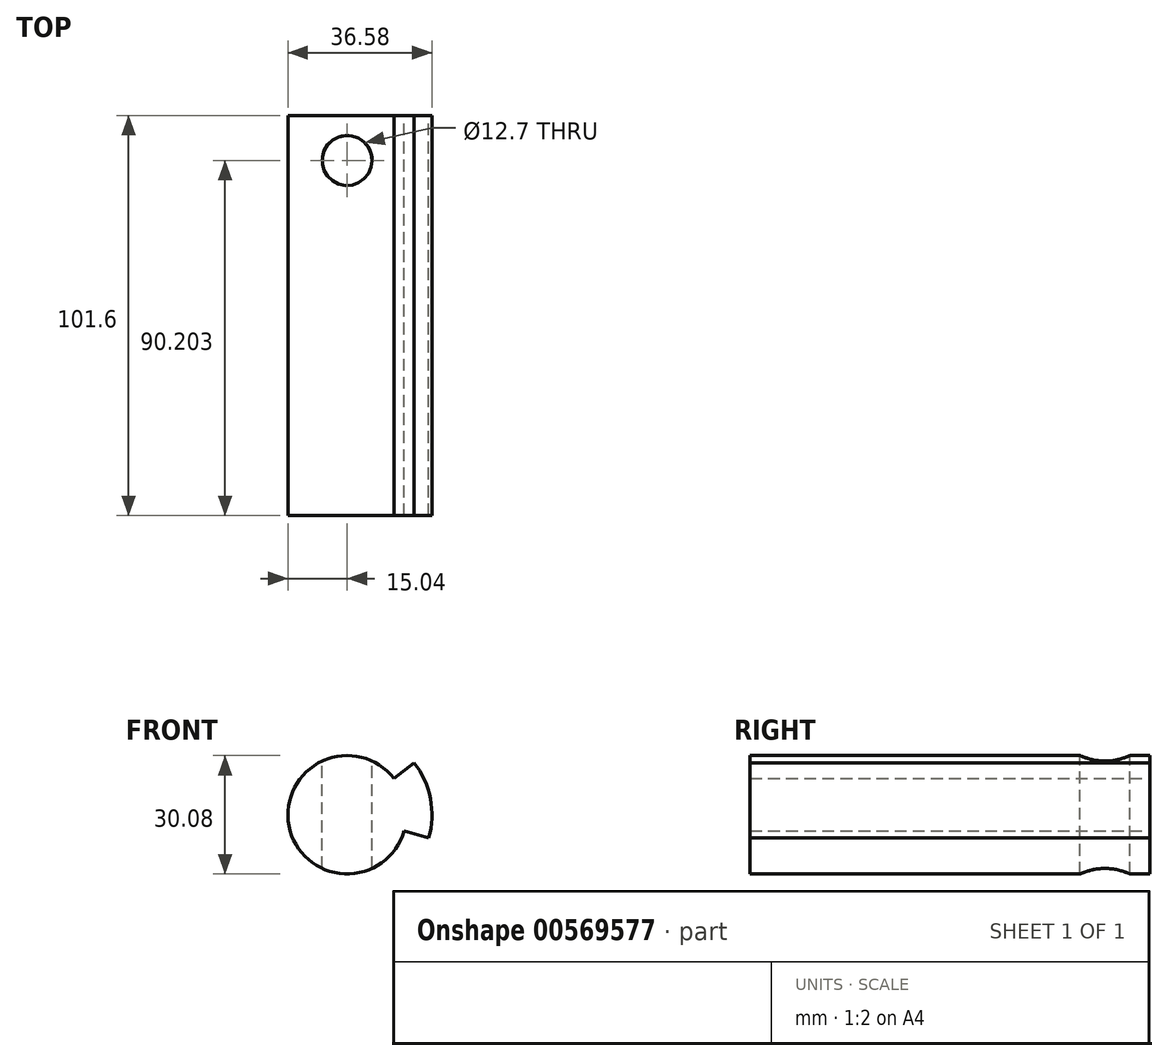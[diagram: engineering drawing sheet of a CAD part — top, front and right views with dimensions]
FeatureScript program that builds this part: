
annotation { "Feature Type Name" : "Feature", "Feature Type Description" : "" }
export const myFeature = defineFeature(function(context is Context, id is Id, definition is map)
    precondition{}
    {
        {
            var Q0;
            Q0=qCreatedBy(makeId("Front.planeOp"),FACE);
            var sketch = newSketch(context, id + "F0", { "sketchPlane" : qUnion([Q0])});
            skArc(sketch, "E0", {"start": v(11.89, 9.2) * mm, "mid": v(-14.76, -2.85) * mm, "end": v(14.46, -4.13) * mm});
            skArc(sketch, "E1.0", {"start": v(20.71, -5.91) * mm, "mid": v(21.15, 4.08) * mm, "end": v(17.03, 13.2) * mm});
            skLineSegment(sketch, "E2", {"start": v(11.89, 9.2) * mm, "end": v(17.03, 13.2) * mm});
            skLineSegment(sketch, "E3", {"start": v(14.46, -4.13) * mm, "end": v(20.71, -5.91) * mm});
            skSolve(sketch);
        }
        {
            var Q0;
            Q0=makeQuery(id+"F0.imprint","IMPRINT",FACE,{"disambiguationData":[TD([[makeQuery(id+"F0.imprint","IMPRINT",EDGE,{"derivedFrom":sQuery(id+"F0.wireOp",EDGE,"E0")}),1.0]])]});
            extrude(context, id + "F1", {"entities" : qUnion([Q0]), "endBound" : BoundingType.SYMMETRIC, "depth" : 101.6 * mm, "offsetDistance" : 25.4 * mm});
        }
        {
            var Q0;
            Q0=qCreatedBy(makeId("Top.planeOp"),FACE);
            var sketch = newSketch(context, id + "F2", { "sketchPlane" : qUnion([Q0])});
            skCircle(sketch, "E4", {"center": v(0, 39.4) * mm, "radius": 6.35 * mm});
            skLineSegment(sketch, "E5", {"start": v(-15.04, -50.8) * mm, "end": v(-15.04, 50.8) * mm});
            skSolve(sketch);
        }
        {
            var Q0;
            Q0 = qSketchRegion(id + "F2", true);
            extrude(context, id + "F3", {"entities" : qUnion([Q0]), "operationType" : NewBodyOperationType.REMOVE, "endBound" : BoundingType.THROUGH_ALL, "oppositeDirection" : true, "depth" : 25.4 * mm, "offsetDistance" : 25.4 * mm, "hasSecondDirection" : true, "secondDirectionOppositeDirection" : false, "secondDirectionDepth" : 25.4 * mm});
        }
    });
